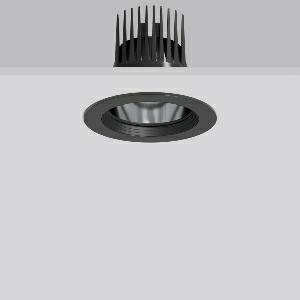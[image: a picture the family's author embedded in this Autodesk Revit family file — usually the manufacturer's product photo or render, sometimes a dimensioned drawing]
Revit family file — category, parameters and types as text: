
# Revit family: heledon_maxi_e_901759_003_04bf
name_source: partatom
category: Lighting Fixtures
units: mm (PartAtom-declared; Revit-internal decimal feet)

## family parameters
Cut with Voids When Loaded = No
Host = Face
Light Source = No
Part Type = Normal
Room Calculation Point = No
Round Connector Dimension = Use Diameter
Shared = No

## types (1)
- HELEDON maxi E (1 x LED Modul 930, 3250 lm, 3000)
    Apparent Load = 25 VA
    Approval mark = CE
    CIE Flux Codes = 97 100 100 100 100
    Color Rendering = 90
    Color Temperature = 3000
    Default Elevation = 1800 mm
    Description = Series: HELEDON maxi
Round recessed downlight. Housing: die-cast aluminium, powder-coated. Black plastic ring and recessed LED to prevent glare from the side. Optical assembly with reflector made of MIRO-Silver with 98% total light reflection for outstanding efficiency - can be changed without tools. Best colour rendering index Ra>90. Suitable for Recessed ceiling mounting. Installation without tools thanks to spring fastening system. Including separate LED converter with connecting cable 600 mm.High quality converter without flickering and stroboscopic effect. Through-wiring box (5 pole) available as accessory. The following accessories can be mounted without use of tools: interchangeable lenses, decorative glasses, honeycomb louvre, clear and frosted diffusers, white interchangeable plastic ring. 
Colour: deep black, matt (RAL 9005)
Diameter: 162 mm
Height: 3 mm
Cut-out diameter: 152 mm
Recess height: 200 mm
Luminaire: recess height: 135 mm
Lamp: LED
Socket: without socket
Colour temperature: 3000K
Colour rendering index (CRI): 92
System power: 25 W
Rated luminous flux: 3250 lm
Luminous efficiency: 130 lm/W
Control gear: Regulated power supply
Protection class: II
Type of protection: IP 20
    Height = 0 mm  [stored 0 ft]
    Lamp = 1 x LED Modul 930
    Lamp Light Flux = 3250 lm
    Lamp count = 1
    Length = 162 mm
    Lifetime = 50000 h
    Luminous efficacy = 130 lm/W
    Manufacturer = RZB
    ModVariant = No
    Model = 901759.003
    Mounting Place = Ceiling
    Mounting Type = Recessed
    Number of Poles = 1
    OnlyDefault = Yes
    Power Factor = 1
    Product Name = HELEDON maxi E
    Product group = Recessed downlights
    ProductGroupID = 402
    Protection Class = Protection class II
    Protection Degree = IP 20
    RLX_Detail_Level = 1
    RLX_Emergency_Light_Flux = 0 lm
    RLX_Emergency_Type = 0
    RLX_Emergency_Type_DB = No
    RlxData = <blob elided: 120949 chars, md5=71d9ec96>
    Socket = socket
    Standby Power = 0 W
    System Light Flux = 3250 lm
    System Power = 25 W
    Type Comments = Product without accessories
    Type Image = 901662.003.jpg
    URL = http://relux.com
    VarID = ---
    Voltage = 230 V
    Voltage Range = 220-240 V
    Weight = 0.00 kg
    Width = 0 mm  [stored 0 ft]

note: [stored X ft] marks values corroborated as IEEE doubles in the binary element streams (Revit-internal decimal feet)

## geometry (parser evidence)
native form markers: Blend x4, Sweep x13
no freeform markers — native parametric forms only
